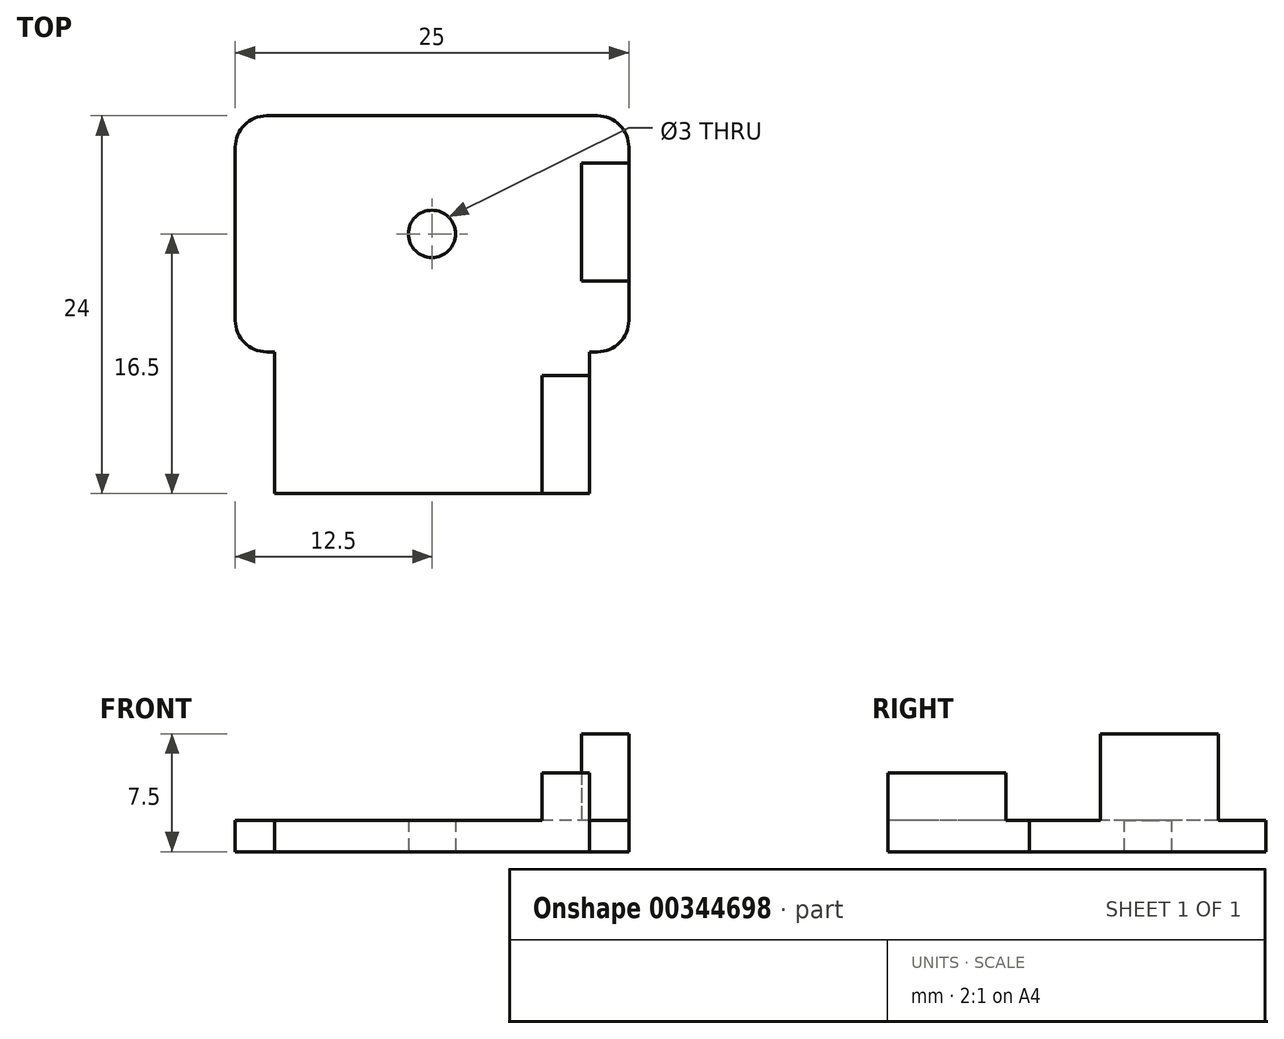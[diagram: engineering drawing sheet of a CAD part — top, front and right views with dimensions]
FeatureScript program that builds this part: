
annotation { "Feature Type Name" : "Feature", "Feature Type Description" : "" }
export const myFeature = defineFeature(function(context is Context, id is Id, definition is map)
    precondition{}
    {
        {
            var Q0;
            Q0=qCreatedBy(makeId("Top.planeOp"),FACE);
            var sketch = newSketch(context, id + "F0", { "sketchPlane" : qUnion([Q0])});
            skLineSegment(sketch, "E0", {"start": v(0, 12) * mm, "end": v(12.5, 12) * mm});
            skLineSegment(sketch, "E1", {"start": v(12.5, 12) * mm, "end": v(12.5, -3) * mm});
            skLineSegment(sketch, "E2", {"start": v(12.5, -3) * mm, "end": v(10, -3) * mm});
            skLineSegment(sketch, "E3", {"start": v(10, -3) * mm, "end": v(10, -12) * mm});
            skLineSegment(sketch, "E4", {"start": v(10, -12) * mm, "end": v(0, -12) * mm});
            skLineSegment(sketch, "E5.MirrorCS", {"start": v(-10, -3) * mm, "end": v(-10, -12) * mm});
            skLineSegment(sketch, "E6.MirrorCS", {"start": v(-12.5, 12) * mm, "end": v(-12.5, -3) * mm});
            skLineSegment(sketch, "E7.MirrorCS", {"start": v(0, 12) * mm, "end": v(-12.5, 12) * mm});
            skLineSegment(sketch, "E8.MirrorCS", {"start": v(-10, -12) * mm, "end": v(0, -12) * mm});
            skLineSegment(sketch, "E9.MirrorCS", {"start": v(-12.5, -3) * mm, "end": v(-10, -3) * mm});
            skCircle(sketch, "E10", {"center": v(0, 4.5) * mm, "radius": 1.5 * mm});
            skSolve(sketch);
        }
        {
            var Q0;
            Q0=makeQuery(id+"F0.imprint","IMPRINT",FACE,{"disambiguationData":[TD([[makeQuery(id+"F0.imprint","IMPRINT",EDGE,{"derivedFrom":sQuery(id+"F0.wireOp",EDGE,"E0")}),-1.0]])]});
            extrude(context, id + "F1", {"entities" : qUnion([Q0]), "depth" : 2 * mm});
        }
        {
            var Q0;
            Q0=makeQuery(id+"F1.opExtrude","CAP_FACE",FACE,{"disambiguationData":[OSD([sQuery(id+"F0.wireOp",EDGE,"E0"),sQuery(id+"F0.wireOp",EDGE,"E1"),sQuery(id+"F0.wireOp",EDGE,"E2"),sQuery(id+"F0.wireOp",EDGE,"E3"),sQuery(id+"F0.wireOp",EDGE,"E4"),sQuery(id+"F0.wireOp",EDGE,"E5.MirrorCS"),sQuery(id+"F0.wireOp",EDGE,"E6.MirrorCS"),sQuery(id+"F0.wireOp",EDGE,"E7.MirrorCS"),sQuery(id+"F0.wireOp",EDGE,"E8.MirrorCS"),sQuery(id+"F0.wireOp",EDGE,"E9.MirrorCS"),sQuery(id+"F0.wireOp",EDGE,"E10")])],"isStart":false});
            var sketch = newSketch(context, id + "F2", { "sketchPlane" : qUnion([Q0])});
            skLineSegment(sketch, "E11.bottom", {"start": v(12.5, 9) * mm, "end": v(9.5, 9) * mm});
            skLineSegment(sketch, "E11.top", {"start": v(12.5, 1.5) * mm, "end": v(9.5, 1.5) * mm});
            skLineSegment(sketch, "E11.left", {"start": v(12.5, 9) * mm, "end": v(12.5, 1.5) * mm});
            skLineSegment(sketch, "E11.right", {"start": v(9.5, 9) * mm, "end": v(9.5, 1.5) * mm});
            skLineSegment(sketch, "E12.bottom", {"start": v(10, -4.5) * mm, "end": v(7, -4.5) * mm});
            skLineSegment(sketch, "E12.top", {"start": v(10, -12) * mm, "end": v(7, -12) * mm});
            skLineSegment(sketch, "E12.left", {"start": v(10, -4.5) * mm, "end": v(10, -12) * mm});
            skLineSegment(sketch, "E12.right", {"start": v(7, -4.5) * mm, "end": v(7, -12) * mm});
            skSolve(sketch);
        }
        {
            var Q0;
            Q0=makeQuery(id+"F2.imprint","IMPRINT",FACE,{"disambiguationData":[TD([[makeQuery(id+"F2.imprint","IMPRINT",EDGE,{"derivedFrom":sQuery(id+"F2.wireOp",EDGE,"E12.bottom")}),1.0]])]});
            extrude(context, id + "F3", {"entities" : qUnion([Q0]), "operationType" : NewBodyOperationType.ADD, "depth" : 3 * mm});
        }
        {
            var Q0;
            Q0=makeQuery(id+"F2.imprint","IMPRINT",FACE,{"disambiguationData":[TD([[makeQuery(id+"F2.imprint","IMPRINT",EDGE,{"derivedFrom":sQuery(id+"F2.wireOp",EDGE,"E11.bottom")}),1.0]])]});
            extrude(context, id + "F4", {"entities" : qUnion([Q0]), "operationType" : NewBodyOperationType.ADD, "depth" : 5.5 * mm});
        }
        {
            var Q0;
            Q0=makeQuery(id+"F1.opExtrude","SWEPT_EDGE",EDGE,{"disambiguationData":[OSD([sQuery(id+"F0.wireOp",EDGE,"E0"),sQuery(id+"F0.wireOp",EDGE,"E1")])]});
            var Q1;
            Q1=makeQuery(id+"F1.opExtrude","SWEPT_EDGE",EDGE,{"disambiguationData":[OSD([sQuery(id+"F0.wireOp",EDGE,"E1"),sQuery(id+"F0.wireOp",EDGE,"E2")])]});
            var Q2;
            Q2=makeQuery(id+"F1.opExtrude","SWEPT_EDGE",EDGE,{"disambiguationData":[OSD([sQuery(id+"F0.wireOp",EDGE,"E6.MirrorCS"),sQuery(id+"F0.wireOp",EDGE,"E9.MirrorCS")])]});
            var Q3;
            Q3=makeQuery(id+"F1.opExtrude","SWEPT_EDGE",EDGE,{"disambiguationData":[OSD([sQuery(id+"F0.wireOp",EDGE,"E6.MirrorCS"),sQuery(id+"F0.wireOp",EDGE,"E7.MirrorCS")])]});
            fillet(context, id + "F5", {"entities" : qUnion([Q0, Q1, Q2, Q3]), "radius" : 2 * mm, "tangentPropagation" : true, "allowEdgeOverflow" : false});
        }
    });
